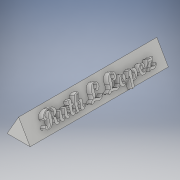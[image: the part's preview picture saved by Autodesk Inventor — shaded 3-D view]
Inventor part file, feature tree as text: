
AUTODESK INVENTOR PART (.ipt)
format: ipt  version: 2018.2 (Build 222227000, 227)  size: 596,480 bytes
history: native  units: in
note: dims shown in document units (in); Inventor stores cm internally (conversion verified against a paired STEP export)
features: extrude x2, sketch x2
ambient origin geometry x8: Origin, YZ Plane, XZ Plane, XY Plane, X Axis, Y Axis, Z Axis, Center Point
bodies: Solid1 (feature_tree)
feature tree (4):
  extrude  "Extrusion1"  Depth=1.0in
  extrude  "Extrusion2"  Depth=0.25in TaperAngle=0.0deg
  sketch  "Sketch1"  dims[d0=0.5in d1=1.0in]
  sketch  "Sketch2"  dims[d2=6.0in d3=0.0in d4=0.25in d5=0.0in]
